# Revit family: FP_Revit_18_RS36W80LJ1_N_Fridge_90001169A
name_source: partatom
category: Specialty Equipment
revit_build: Autodesk Revit 2018 (Build: 20170223_1515(x64)
units: mm (PartAtom-declared; Revit-internal decimal feet)

## family parameters
Always vertical = Yes
Cut with Voids When Loaded = Yes
OmniClass Number = 23.40.40.11.11.17
OmniClass Title = Refrigerator-Freezer
Part Type = Normal
Room Calculation Point = No
Round Connector Dimension = Use Diameter
Shared = No
Work Plane-Based = No

## types (1)
- FP_Revit_18_RS36W80LJ1_N_Fridge_90001169A
    Cavity - Depth = 635 mm
    Cavity - Height = 2032 mm
    Cavity - Width = 914 mm  [stored 2.99869 ft]
    Chassis - Depth = 606 mm  [stored 1.98819 ft]
    Chassis - Height = 1970 mm  [stored 6.46325 ft]
    Chassis - Width = 890 mm  [stored 2.91995 ft]
    Connector Description - Electrical = 115 V, 60Hz, 10 A, fused electrical supply
    Connector Description - Water = 1/4" (6mm) comp. stainless steel braided hose
    Description = 36" Integrated Refrigerator Freezer, Ice
    Handle Style - Contemporary Round (25380 AHS-ASBI-B) = No
    Handle Style - Contemporary Square (RS36W) = No
    Handle Style - Contemporary Square Fine (AHD5RD36W) = No
    Handle Style - Contemporary Square Fine Black (AHD5RD36WB) = No
    Handle Style - Professional Round (AHCRS36W) = No
    Handle Style - Professional Round Flush (AHP3RD36W) = No
    Handle Style - Professional Square (AHV2RS36W) = No
    Manufacturer = Fisher & Paykel Appliances
    Material - Body = Fisher & Paykel - Grey
    Material - Door Front = Fisher & Paykel - Stainless Steel
    Material - Door Structure = Fisher & Paykel - White
    Model = RS36W80LJ1_N
    Product - Depth = 606 mm  [stored 1.98819 ft]
    Product - Height = 2028 mm  [stored 6.65354 ft]
    Product - Width = 906 mm  [stored 2.97244 ft]
    Stainless Steel Door Panels (RD3680WL) = No
    URL = www.fisherpaykel.com
    Visibility - Clearance Required = Yes
    Visibility - Visibility Control Note = Yes

note: [stored X ft] marks values corroborated as IEEE doubles in the binary element streams (Revit-internal decimal feet)

## geometry (parser evidence)
native form markers: Sweep x30
no freeform markers — native parametric forms only
